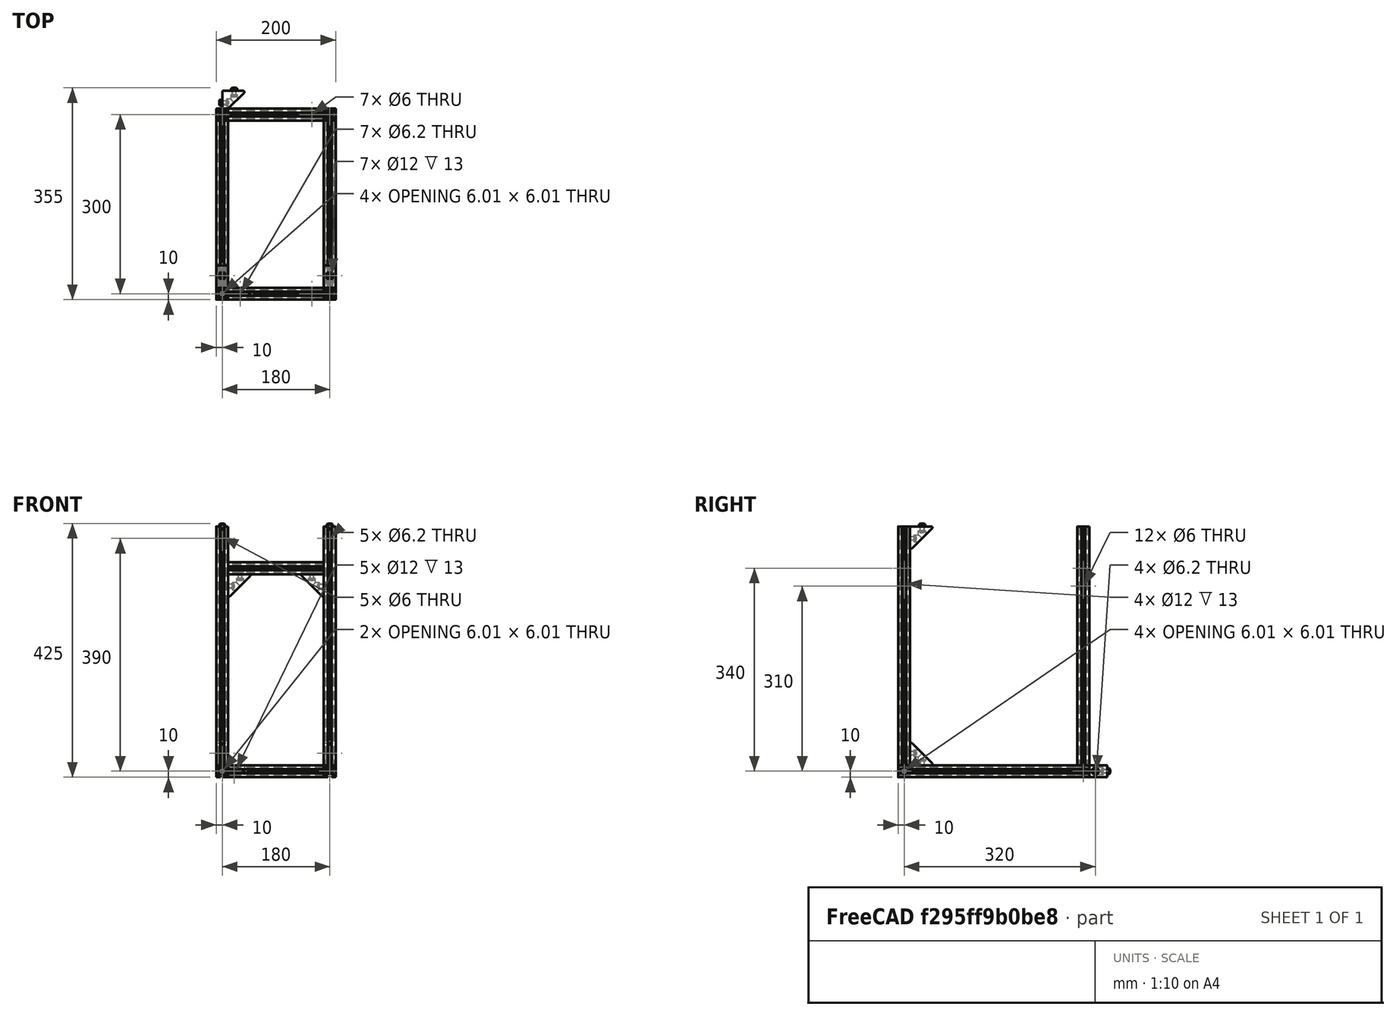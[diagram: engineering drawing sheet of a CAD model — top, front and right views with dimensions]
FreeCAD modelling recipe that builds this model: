
FCSTD DOCUMENT  (FreeCAD 0.17R9796 (Git))
Label: UPKframe5
License: All rights reserved
LicenseURL: http://en.wikipedia.org/wiki/All_rights_reserved
objects: Part::Feature×64, Part::FeaturePython×18, App::Part×7, Part::Compound×7
note: 89 computed .brp shape members not serialized (recipe doc carries the construction recipe); baked Part::Feature solids carry a one-line shape summary decoded from their .brp

FEATURE [Part::Feature] Pocket001001  label="tslot40"
  Placement = pos=(0,0,20) rot=(0,0,1;0rad)
  shape: bbox 20 x 20 x 400 mm, 94 faces (baked)
FEATURE [Part::Feature] Pocket003001  label="tslot32con"
  Placement = pos=(0,10,10) rot=(1,0,0;1.5708rad)
  shape: bbox 20 x 320 x 20 mm, 150 faces (baked)
FEATURE [Part::Feature] Pocket003002  label="tslot16"
  Placement = pos=(10,0,10) rot=(0,1,0;1.5708rad)
  shape: bbox 160 x 20 x 20 mm, 94 faces (baked)
FEATURE [Part::Feature] Pocket003006  label="tslot16_001"
  Placement = pos=(10,-300,10) rot=(0,1,0;1.5708rad)
  shape: bbox 160 x 20 x 20 mm, 94 faces (baked)
FEATURE [Part::Feature] Pocket003007  label="tslot32con_001"
  Placement = pos=(180,-310,10) rot=(0,0.707107,0.707107;3.14159rad)
  shape: bbox 20 x 320 x 20 mm, 150 faces (baked)
FEATURE [Part::FeaturePython] Screw  label="M6x25-Screw"  # Fasteners workbench fastener (typed FeaturePython)
  Placement = pos=(-4,0,10) rot=(0,-1,0;1.5708rad)
  diameter = 7
  invert = false
  length = 6
  matchOuter = false
  offset = 0
  thread = false
  type = 15
FEATURE [Part::FeaturePython] Screw001  label="M6x25-Screw004"  # Fasteners workbench fastener (typed FeaturePython)
  Placement = pos=(-4,-300,10) rot=(0,-1,0;1.5708rad)
  diameter = 7
  invert = false
  length = 6
  matchOuter = false
  offset = 0
  thread = false
  type = 15
FEATURE [Part::FeaturePython] Screw002  label="M6x25-Screw005"  # Fasteners workbench fastener (typed FeaturePython)
  Placement = pos=(184,0,10) rot=(0,1,0;1.5708rad)
  diameter = 7
  invert = false
  length = 6
  matchOuter = false
  offset = 0
  thread = false
  type = 15
FEATURE [Part::FeaturePython] Screw004  label="M6x25-Screw006"  # Fasteners workbench fastener (typed FeaturePython)
  Placement = pos=(184,-300,10) rot=(0,1,0;1.5708rad)
  diameter = 7
  invert = false
  length = 6
  matchOuter = false
  offset = 0
  thread = false
  type = 15
FEATURE [App::Part] Part  label="lower_frame"
  Group = -> [Pocket003001,Pocket003002,Pocket003006,Pocket003007,Screw,Screw001,Screw002,Screw004]
  License = CC BY 3.0
  LicenseURL = http://creativecommons.org/licenses/by/3.0/
  Origin = -> PartOrigin
FEATURE [Part::Feature] Pocket003008  label="tslot32con001"
  Placement = pos=(0,10,10) rot=(1,0,0;1.5708rad)
  shape: bbox 20 x 320 x 20 mm, 150 faces (baked)
FEATURE [Part::Feature] Pocket003009  label="tslot041"
  Placement = pos=(10,0,10) rot=(0,1,0;1.5708rad)
  shape: bbox 160 x 20 x 20 mm, 94 faces (baked)
FEATURE [Part::Feature] Pocket003010  label="tslot16_002"
  Placement = pos=(10,-300,10) rot=(0,1,0;1.5708rad)
  shape: bbox 160 x 20 x 20 mm, 94 faces (baked)
FEATURE [Part::Feature] Pocket003011  label="tslot32con_002"
  Placement = pos=(180,-310,10) rot=(0,0.707107,0.707107;3.14159rad)
  shape: bbox 20 x 320 x 20 mm, 150 faces (baked)
FEATURE [Part::FeaturePython] Screw005  label="M6x25-Screw007"  # Fasteners workbench fastener (typed FeaturePython)
  Placement = pos=(-4,0,10) rot=(0,-1,0;1.5708rad)
  diameter = 7
  invert = false
  length = 6
  matchOuter = false
  offset = 0
  thread = false
  type = 15
FEATURE [Part::FeaturePython] Screw006  label="M6x25-Screw008"  # Fasteners workbench fastener (typed FeaturePython)
  Placement = pos=(-4,-300,10) rot=(0,-1,0;1.5708rad)
  diameter = 7
  invert = false
  length = 6
  matchOuter = false
  offset = 0
  thread = false
  type = 15
FEATURE [Part::FeaturePython] Screw007  label="M6x25-Screw009"  # Fasteners workbench fastener (typed FeaturePython)
  Placement = pos=(184,0,10) rot=(0,1,0;1.5708rad)
  diameter = 7
  invert = false
  length = 6
  matchOuter = false
  offset = 0
  thread = false
  type = 15
FEATURE [Part::FeaturePython] Screw008  label="M6x25-Screw010"  # Fasteners workbench fastener (typed FeaturePython)
  Placement = pos=(184,-300,10) rot=(0,1,0;1.5708rad)
  diameter = 7
  invert = false
  length = 6
  matchOuter = false
  offset = 0
  thread = false
  type = 15
FEATURE [App::Part] Part001  label="upper_frame"
  Group = -> [Pocket003008,Pocket003009,Pocket003010,Pocket003011,Screw005,Screw006,Screw007,Screw008]
  License = CC BY 3.0
  LicenseURL = http://creativecommons.org/licenses/by/3.0/
  Origin = -> PartOrigin001
  Placement = pos=(0,0,420) rot=(0,0,1;0rad)
FEATURE [Part::Feature] Pocket003012  label="tslot042"
  Placement = pos=(180,0,20) rot=(0,0,1;0rad)
  shape: bbox 20 x 20 x 400 mm, 94 faces (baked)
FEATURE [Part::Feature] Pocket003013  label="tslot043"
  Placement = pos=(180,-300,20) rot=(0,0,1;0rad)
  shape: bbox 20 x 20 x 400 mm, 94 faces (baked)
FEATURE [Part::Feature] Pocket003014  label="tslot044"
  Placement = pos=(0,-300,20) rot=(0,0,1;0rad)
  shape: bbox 20 x 20 x 400 mm, 94 faces (baked)
FEATURE [Part::Feature] Fillet004001  label="Fillet005"
  shape: bbox 37.5 x 37.5 x 20 mm, 26 faces (baked)
FEATURE [Part::FeaturePython] Screw009  label="M6x12-Screw"  # Fasteners workbench fastener (typed FeaturePython)
  Placement = pos=(7,20,10) rot=(0,1,0;1.5708rad)
  diameter = 4
  invert = false
  length = 1
  matchOuter = false
  offset = 0
  thread = false
  type = 20
FEATURE [Part::Feature] Body001  label="m6nutplate"
  Placement = pos=(-1.5,15,5) rot=(0,-1,0;1.5708rad)
  shape: bbox 3 x 10 x 10 mm, 9 faces (baked)
FEATURE [Part::FeaturePython] Screw010  label="M6x12-Screw001"  # Fasteners workbench fastener (typed FeaturePython)
  Placement = pos=(20,33,10) rot=(1,0,0;1.5708rad)
  diameter = 4
  invert = false
  length = 1
  matchOuter = false
  offset = 0
  thread = false
  type = 20
FEATURE [Part::Feature] Body002  label="m6nutplate001"
  Placement = pos=(15,41.5,5) rot=(0.57735,0.57735,0.57735;4.18879rad)
  shape: bbox 10 x 3 x 10 mm, 9 faces (baked)
FEATURE [App::Part] Part002  label="cornerstonescrewnut"
  Group = -> [Body001,Screw009,Fillet004001,Screw010,Body002]
  License = CC BY 3.0
  LicenseURL = http://creativecommons.org/licenses/by/3.0/
  Origin = -> PartOrigin002
  Placement = pos=(10,-50,20) rot=(0,-1,0;1.5708rad)
FEATURE [Part::Feature] Fillet004002  label="Fillet006"
  shape: bbox 37.5 x 37.5 x 20 mm, 26 faces (baked)
FEATURE [Part::FeaturePython] Screw011  label="M6x12-Screw002"  # Fasteners workbench fastener (typed FeaturePython)
  Placement = pos=(7,20,10) rot=(0,1,0;1.5708rad)
  diameter = 4
  invert = false
  length = 1
  matchOuter = false
  offset = 0
  thread = false
  type = 20
FEATURE [Part::Feature] Body003  label="m6nutplate002"
  Placement = pos=(-1.5,15,5) rot=(0,-1,0;1.5708rad)
  shape: bbox 3 x 10 x 10 mm, 9 faces (baked)
FEATURE [Part::FeaturePython] Screw012  label="M6x12-Screw003"  # Fasteners workbench fastener (typed FeaturePython)
  Placement = pos=(20,33,10) rot=(1,0,0;1.5708rad)
  diameter = 4
  invert = false
  length = 1
  matchOuter = false
  offset = 0
  thread = false
  type = 20
FEATURE [Part::Feature] Body004  label="m6nutplate003"
  Placement = pos=(15,41.5,5) rot=(0.57735,0.57735,0.57735;4.18879rad)
  shape: bbox 10 x 3 x 10 mm, 9 faces (baked)
FEATURE [App::Part] Part003  label="cornerstonescrewnut001"
  Group = -> [Body003,Screw011,Fillet004002,Screw012,Body004]
  License = CC BY 3.0
  LicenseURL = http://creativecommons.org/licenses/by/3.0/
  Origin = -> PartOrigin003
  Placement = pos=(190,-50,20) rot=(0,-1,0;1.5708rad)
FEATURE [Part::Feature] Fillet004003  label="Fillet007"
  shape: bbox 37.5 x 37.5 x 20 mm, 26 faces (baked)
FEATURE [Part::FeaturePython] Screw013  label="M6x12-Screw004"  # Fasteners workbench fastener (typed FeaturePython)
  Placement = pos=(7,20,10) rot=(0,1,0;1.5708rad)
  diameter = 4
  invert = false
  length = 1
  matchOuter = false
  offset = 0
  thread = false
  type = 20
FEATURE [Part::Feature] Body005  label="m6nutplate004"
  Placement = pos=(-1.5,15,5) rot=(0,-1,0;1.5708rad)
  shape: bbox 3 x 10 x 10 mm, 9 faces (baked)
FEATURE [Part::FeaturePython] Screw014  label="M6x12-Screw005"  # Fasteners workbench fastener (typed FeaturePython)
  Placement = pos=(20,33,10) rot=(1,0,0;1.5708rad)
  diameter = 4
  invert = false
  length = 1
  matchOuter = false
  offset = 0
  thread = false
  type = 20
FEATURE [Part::Feature] Body006  label="m6nutplate005"
  Placement = pos=(15,41.5,5) rot=(0.57735,0.57735,0.57735;4.18879rad)
  shape: bbox 10 x 3 x 10 mm, 9 faces (baked)
FEATURE [App::Part] Part004  label="cornerstonescrewnut002"
  Group = -> [Body005,Screw013,Fillet004003,Screw014,Body006]
  License = CC BY 3.0
  LicenseURL = http://creativecommons.org/licenses/by/3.0/
  Origin = -> PartOrigin004
  Placement = pos=(-10,-50,420) rot=(0,1,0;1.5708rad)
FEATURE [Part::Feature] Fillet004004  label="Fillet008"
  shape: bbox 37.5 x 37.5 x 20 mm, 26 faces (baked)
FEATURE [Part::FeaturePython] Screw015  label="M6x12-Screw006"  # Fasteners workbench fastener (typed FeaturePython)
  Placement = pos=(7,20,10) rot=(0,1,0;1.5708rad)
  diameter = 4
  invert = false
  length = 1
  matchOuter = false
  offset = 0
  thread = false
  type = 20
FEATURE [Part::Feature] Body007  label="m6nutplate006"
  Placement = pos=(-1.5,15,5) rot=(0,-1,0;1.5708rad)
  shape: bbox 3 x 10 x 10 mm, 9 faces (baked)
FEATURE [Part::FeaturePython] Screw016  label="M6x12-Screw007"  # Fasteners workbench fastener (typed FeaturePython)
  Placement = pos=(20,33,10) rot=(1,0,0;1.5708rad)
  diameter = 4
  invert = false
  length = 1
  matchOuter = false
  offset = 0
  thread = false
  type = 20
FEATURE [Part::Feature] Body008  label="m6nutplate007"
  Placement = pos=(15,41.5,5) rot=(0.57735,0.57735,0.57735;4.18879rad)
  shape: bbox 10 x 3 x 10 mm, 9 faces (baked)
FEATURE [App::Part] Part005  label="cornerstonescrewnut003"
  Group = -> [Body007,Screw015,Fillet004004,Screw016,Body008]
  License = CC BY 3.0
  LicenseURL = http://creativecommons.org/licenses/by/3.0/
  Origin = -> PartOrigin005
  Placement = pos=(170,-50,420) rot=(0,1,0;1.5708rad)
FEATURE [Part::Feature] Fillet004005  label="Fillet009"
  shape: bbox 37.5 x 37.5 x 20 mm, 26 faces (baked)
FEATURE [Part::FeaturePython] Screw017  label="M6x12-Screw008"  # Fasteners workbench fastener (typed FeaturePython)
  Placement = pos=(7,20,10) rot=(0,1,0;1.5708rad)
  diameter = 4
  invert = false
  length = 1
  matchOuter = false
  offset = 0
  thread = false
  type = 20
FEATURE [Part::Feature] Body009  label="m6nutplate008"
  Placement = pos=(-1.5,15,5) rot=(0,-1,0;1.5708rad)
  shape: bbox 3 x 10 x 10 mm, 9 faces (baked)
FEATURE [Part::FeaturePython] Screw018  label="M6x12-Screw009"  # Fasteners workbench fastener (typed FeaturePython)
  Placement = pos=(20,33,10) rot=(1,0,0;1.5708rad)
  diameter = 4
  invert = false
  length = 1
  matchOuter = false
  offset = 0
  thread = false
  type = 20
FEATURE [Part::Feature] Body010  label="m6nutplate009"
  Placement = pos=(15,41.5,5) rot=(0.57735,0.57735,0.57735;4.18879rad)
  shape: bbox 10 x 3 x 10 mm, 9 faces (baked)
FEATURE [App::Part] Part006  label="cornerstonescrewnut004"
  Group = -> [Body009,Screw017,Fillet004005,Screw018,Body010]
  License = CC BY 3.0
  LicenseURL = http://creativecommons.org/licenses/by/3.0/
  Origin = -> PartOrigin006
  Placement = pos=(10,10,300) rot=(1,0,0;1.5708rad)
FEATURE [Part::Feature] Body009001  label="m6nutplate010"
  Placement = pos=(-1.5,15,5) rot=(0,-1,0;1.5708rad)
  shape: bbox 3 x 10 x 10 mm, 9 faces (baked)
FEATURE [Part::Feature] Body010001  label="m6nutplate011"
  Placement = pos=(15,41.5,5) rot=(0.57735,0.57735,0.57735;4.18879rad)
  shape: bbox 10 x 3 x 10 mm, 9 faces (baked)
FEATURE [Part::Feature] Screw018001  label="M6x12-Screw010"
  Placement = pos=(20,33,10) rot=(1,0,0;1.5708rad)
  shape: bbox 10.5 x 15.3 x 10.5 mm, 15 faces (baked)
FEATURE [Part::Feature] Screw017001  label="M6x12-Screw011"
  Placement = pos=(7,20,10) rot=(0,1,0;1.5708rad)
  shape: bbox 15.3 x 10.5 x 10.5 mm, 15 faces (baked)
FEATURE [Part::Feature] Fillet004005001  label="Fillet010"
  shape: bbox 37.5 x 37.5 x 20 mm, 26 faces (baked)
FEATURE [Part::Compound] Compound
  Links = -> [Body009001,Fillet004005001,Screw017001,Body010001,Screw018001]
  Placement = pos=(10,-250,420) rot=(0.707107,0,-0.707107;3.14159rad)
FEATURE [Part::Feature] Body010002  label="m6nutplate012"
  Placement = pos=(-1.5,15,5) rot=(0,-1,0;1.5708rad)
  shape: bbox 3 x 10 x 10 mm, 9 faces (baked)
FEATURE [Part::Feature] Body010003  label="m6nutplate013"
  Placement = pos=(15,41.5,5) rot=(0.57735,0.57735,0.57735;4.18879rad)
  shape: bbox 10 x 3 x 10 mm, 9 faces (baked)
FEATURE [Part::Feature] Screw018002  label="M6x12-Screw012"
  Placement = pos=(20,33,10) rot=(1,0,0;1.5708rad)
  shape: bbox 10.5 x 15.3 x 10.5 mm, 15 faces (baked)
FEATURE [Part::Feature] Screw018003  label="M6x12-Screw013"
  Placement = pos=(7,20,10) rot=(0,1,0;1.5708rad)
  shape: bbox 15.3 x 10.5 x 10.5 mm, 15 faces (baked)
FEATURE [Part::Feature] Fillet004005002  label="Fillet011"
  shape: bbox 37.5 x 37.5 x 20 mm, 26 faces (baked)
FEATURE [Part::Compound] Compound001
  Links = -> [Body010002,Fillet004005002,Screw018003,Body010003,Screw018002]
  Placement = pos=(190,-250,420) rot=(0.707107,0,-0.707107;3.14159rad)
FEATURE [Part::Feature] Body010004  label="m6nutplate014"
  Placement = pos=(-1.5,15,5) rot=(0,-1,0;1.5708rad)
  shape: bbox 3 x 10 x 10 mm, 9 faces (baked)
FEATURE [Part::Feature] Body010005  label="m6nutplate015"
  Placement = pos=(15,41.5,5) rot=(0.57735,0.57735,0.57735;4.18879rad)
  shape: bbox 10 x 3 x 10 mm, 9 faces (baked)
FEATURE [Part::Feature] Screw018004  label="M6x12-Screw014"
  Placement = pos=(20,33,10) rot=(1,0,0;1.5708rad)
  shape: bbox 10.5 x 15.3 x 10.5 mm, 15 faces (baked)
FEATURE [Part::Feature] Screw018005  label="M6x12-Screw015"
  Placement = pos=(7,20,10) rot=(0,1,0;1.5708rad)
  shape: bbox 15.3 x 10.5 x 10.5 mm, 15 faces (baked)
FEATURE [Part::Feature] Fillet004005003  label="Fillet012"
  shape: bbox 37.5 x 37.5 x 20 mm, 26 faces (baked)
FEATURE [Part::Compound] Compound002
  Links = -> [Body010004,Fillet004005003,Screw018005,Body010005,Screw018004]
  Placement = pos=(10,-290,60) rot=(0.57735,0.57735,-0.57735;4.18879rad)
FEATURE [Part::Feature] Body010006  label="m6nutplate016"
  Placement = pos=(-1.5,15,5) rot=(0,-1,0;1.5708rad)
  shape: bbox 3 x 10 x 10 mm, 9 faces (baked)
FEATURE [Part::Feature] Body010007  label="m6nutplate017"
  Placement = pos=(15,41.5,5) rot=(0.57735,0.57735,0.57735;4.18879rad)
  shape: bbox 10 x 3 x 10 mm, 9 faces (baked)
FEATURE [Part::Feature] Screw018006  label="M6x12-Screw016"
  Placement = pos=(20,33,10) rot=(1,0,0;1.5708rad)
  shape: bbox 10.5 x 15.3 x 10.5 mm, 15 faces (baked)
FEATURE [Part::Feature] Screw018007  label="M6x12-Screw017"
  Placement = pos=(7,20,10) rot=(0,1,0;1.5708rad)
  shape: bbox 15.3 x 10.5 x 10.5 mm, 15 faces (baked)
FEATURE [Part::Feature] Fillet004005004  label="Fillet013"
  shape: bbox 37.5 x 37.5 x 20 mm, 26 faces (baked)
FEATURE [Part::Compound] Compound003
  Links = -> [Body010006,Fillet004005004,Screw018007,Body010007,Screw018006]
  Placement = pos=(190,-290,60) rot=(0.57735,0.57735,-0.57735;4.18879rad)
FEATURE [Part::Feature] Pocket003015  label="tslot16_across"
  Placement = pos=(10,0,350) rot=(0,1,0;1.5708rad)
  shape: bbox 160 x 20 x 20 mm, 94 faces (baked)
FEATURE [Part::Feature] Pocket003016  label="tslot16_across001"
  Placement = pos=(10,-300,350) rot=(0,1,0;1.5708rad)
  shape: bbox 160 x 20 x 20 mm, 94 faces (baked)
FEATURE [Part::Feature] Body010008  label="m6nutplate018"
  Placement = pos=(-1.5,15,5) rot=(0,-1,0;1.5708rad)
  shape: bbox 3 x 10 x 10 mm, 9 faces (baked)
FEATURE [Part::Feature] Body010009  label="m6nutplate019"
  Placement = pos=(15,41.5,5) rot=(0.57735,0.57735,0.57735;4.18879rad)
  shape: bbox 10 x 3 x 10 mm, 9 faces (baked)
FEATURE [Part::Feature] Screw018008  label="M6x12-Screw018"
  Placement = pos=(20,33,10) rot=(1,0,0;1.5708rad)
  shape: bbox 10.5 x 15.3 x 10.5 mm, 15 faces (baked)
FEATURE [Part::Feature] Screw018009  label="M6x12-Screw019"
  Placement = pos=(7,20,10) rot=(0,1,0;1.5708rad)
  shape: bbox 15.3 x 10.5 x 10.5 mm, 15 faces (baked)
FEATURE [Part::Feature] Fillet004005005  label="Fillet014"
  shape: bbox 37.5 x 37.5 x 20 mm, 26 faces (baked)
FEATURE [Part::Compound] Compound004
  Links = -> [Body010008,Fillet004005005,Screw018009,Body010009,Screw018008]
  Placement = pos=(10,-290,300) rot=(1,0,0;1.5708rad)
FEATURE [Part::Feature] Body010010  label="m6nutplate020"
  Placement = pos=(-1.5,15,5) rot=(0,-1,0;1.5708rad)
  shape: bbox 3 x 10 x 10 mm, 9 faces (baked)
FEATURE [Part::Feature] Body010011  label="m6nutplate021"
  Placement = pos=(15,41.5,5) rot=(0.57735,0.57735,0.57735;4.18879rad)
  shape: bbox 10 x 3 x 10 mm, 9 faces (baked)
FEATURE [Part::Feature] Screw018010  label="M6x12-Screw020"
  Placement = pos=(20,33,10) rot=(1,0,0;1.5708rad)
  shape: bbox 10.5 x 15.3 x 10.5 mm, 15 faces (baked)
FEATURE [Part::Feature] Screw018011  label="M6x12-Screw021"
  Placement = pos=(7,20,10) rot=(0,1,0;1.5708rad)
  shape: bbox 15.3 x 10.5 x 10.5 mm, 15 faces (baked)
FEATURE [Part::Feature] Fillet004005006  label="Fillet015"
  shape: bbox 37.5 x 37.5 x 20 mm, 26 faces (baked)
FEATURE [Part::Compound] Compound005
  Links = -> [Body010010,Fillet004005006,Screw018011,Body010011,Screw018010]
  Placement = pos=(130,-290,340) rot=(0.57735,0.57735,-0.57735;2.0944rad)
FEATURE [Part::Feature] Body010012  label="m6nutplate022"
  Placement = pos=(-1.5,15,5) rot=(0,-1,0;1.5708rad)
  shape: bbox 3 x 10 x 10 mm, 9 faces (baked)
FEATURE [Part::Feature] Body010013  label="m6nutplate023"
  Placement = pos=(15,41.5,5) rot=(0.57735,0.57735,0.57735;4.18879rad)
  shape: bbox 10 x 3 x 10 mm, 9 faces (baked)
FEATURE [Part::Feature] Screw018012  label="M6x12-Screw022"
  Placement = pos=(20,33,10) rot=(1,0,0;1.5708rad)
  shape: bbox 10.5 x 15.3 x 10.5 mm, 15 faces (baked)
FEATURE [Part::Feature] Screw018013  label="M6x12-Screw023"
  Placement = pos=(7,20,10) rot=(0,1,0;1.5708rad)
  shape: bbox 15.3 x 10.5 x 10.5 mm, 15 faces (baked)
FEATURE [Part::Feature] Fillet004005007  label="Fillet016"
  shape: bbox 37.5 x 37.5 x 20 mm, 26 faces (baked)
FEATURE [Part::Compound] Compound006
  Links = -> [Body010012,Fillet004005007,Screw018013,Body010013,Screw018012]
  Placement = pos=(130,10,340) rot=(0.57735,0.57735,-0.57735;2.0944rad)
